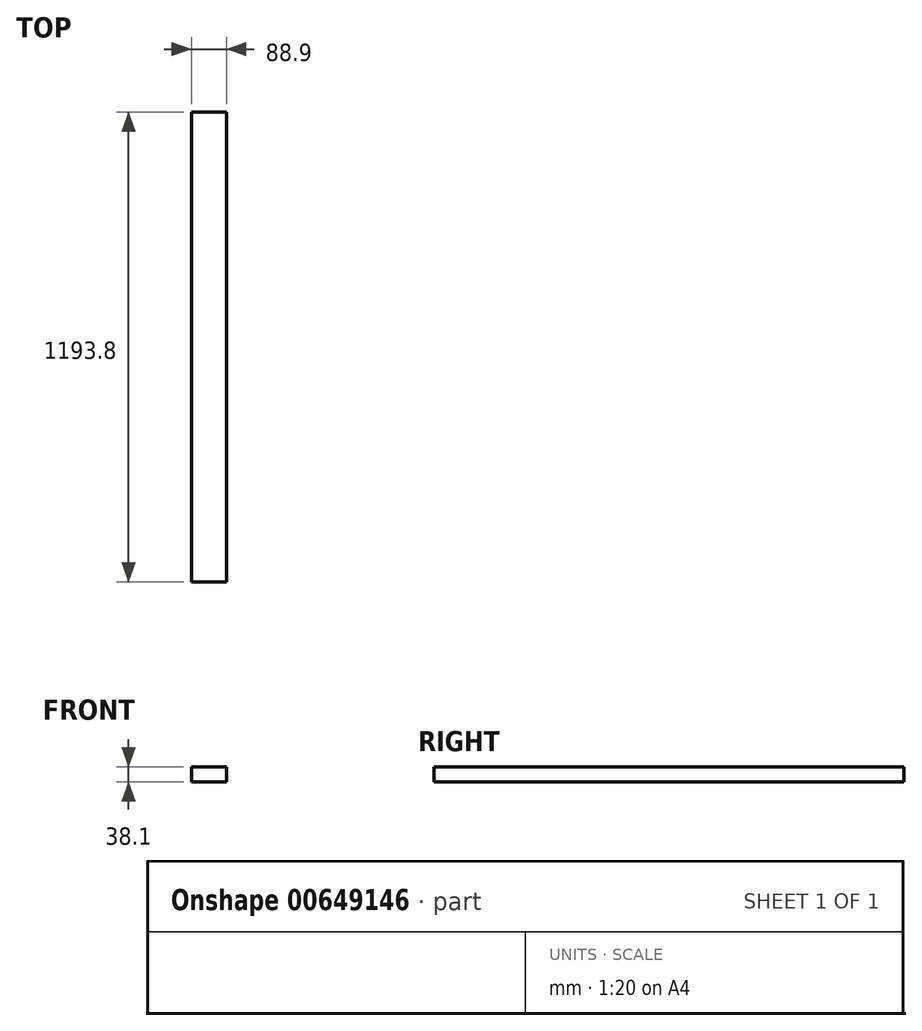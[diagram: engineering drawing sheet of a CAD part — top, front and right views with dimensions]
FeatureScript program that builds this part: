
annotation { "Feature Type Name" : "Feature", "Feature Type Description" : "" }
export const myFeature = defineFeature(function(context is Context, id is Id, definition is map)
    precondition{}
    {
        {
            var Q0;
            Q0=qCreatedBy(makeId("Front.planeOp"),FACE);
            var sketch = newSketch(context, id + "F0", { "sketchPlane" : qUnion([Q0])});
            skLineSegment(sketch, "E0.bottom", {"start": v(0, 0) * mm, "end": v(88.9, 0) * mm});
            skLineSegment(sketch, "E0.top", {"start": v(0, 38.1) * mm, "end": v(88.9, 38.1) * mm});
            skLineSegment(sketch, "E0.left", {"start": v(0, 0) * mm, "end": v(0, 38.1) * mm});
            skLineSegment(sketch, "E0.right", {"start": v(88.9, 0) * mm, "end": v(88.9, 38.1) * mm});
            skSolve(sketch);
        }
        {
            var Q0;
            Q0=qSketchRegion(id+"F0",true);
            extrude(context, id + "F1", {"entities" : qUnion([Q0]), "depth" : 1193.8 * mm, "offsetDistance" : 25.4 * mm});
        }
    });
